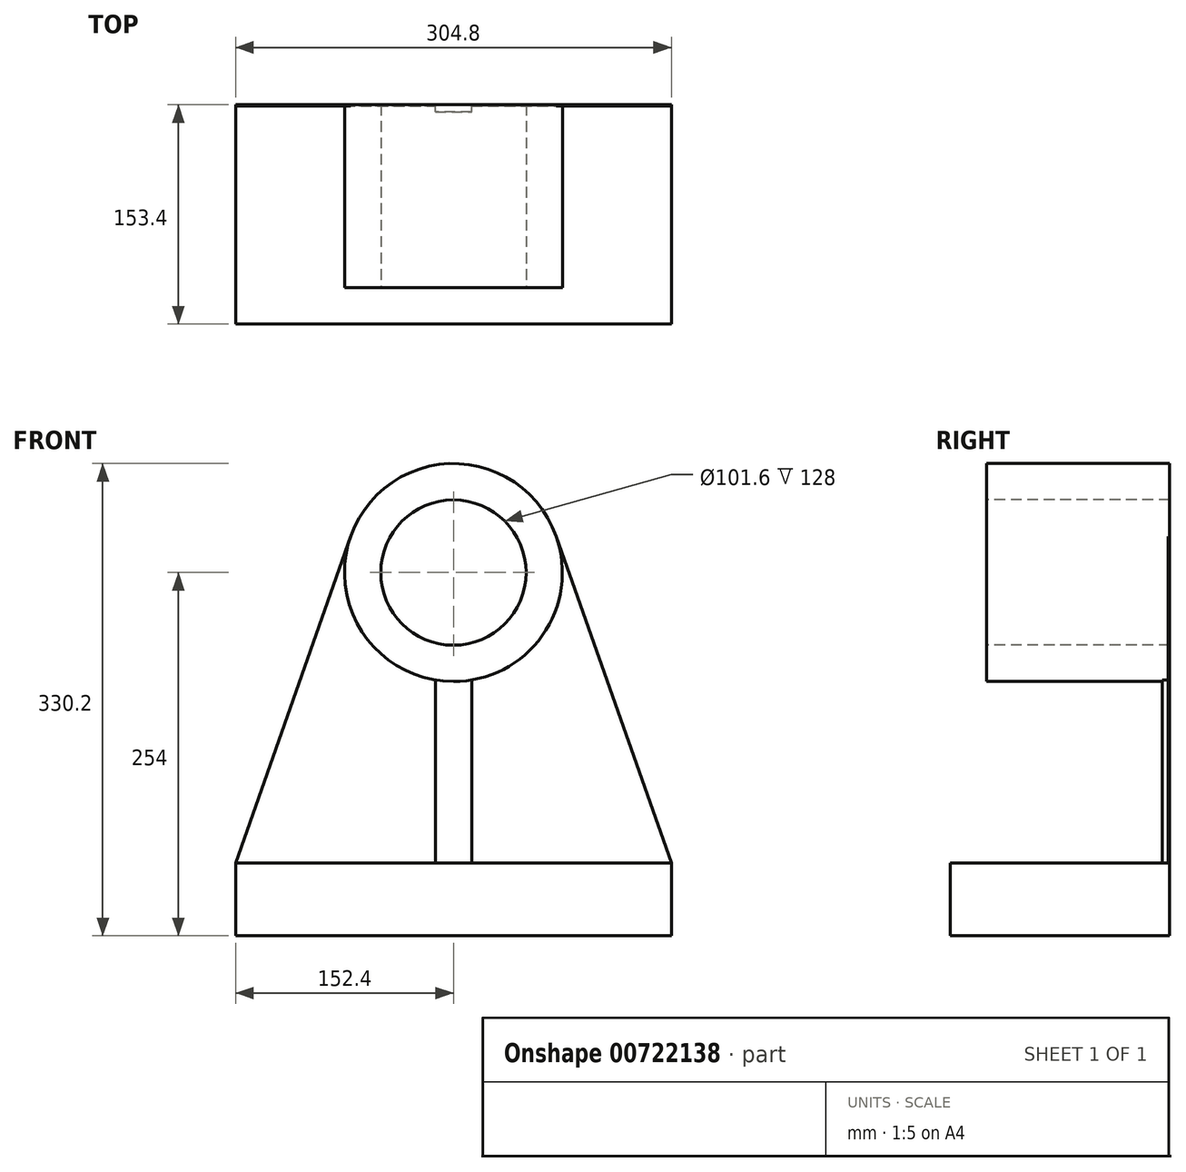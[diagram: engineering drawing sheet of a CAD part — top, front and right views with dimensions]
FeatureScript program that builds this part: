
annotation { "Feature Type Name" : "Feature", "Feature Type Description" : "" }
export const myFeature = defineFeature(function(context is Context, id is Id, definition is map)
    precondition{}
    {
        {
            assignVariable(context, id + "F0", {"name" : "C", "anyValue" : 1});
        }
        {
            var Q0;
            Q0=qCreatedBy(makeId("Front.planeOp"),FACE);
            var sketch = newSketch(context, id + "F1", { "sketchPlane" : qUnion([Q0])});
            skLineSegment(sketch, "E0.bottom", {"start": v(0, 0) * mm, "end": v(-304.8, 0) * mm});
            skLineSegment(sketch, "E0.left", {"start": v(0, 0) * mm, "end": v(0, 50.8) * mm});
            skLineSegment(sketch, "E0.right", {"start": v(-304.8, 0) * mm, "end": v(-304.8, 50.8) * mm});
            skLineSegment(sketch, "E1", {"start": v(0, 50.8) * mm, "end": v(-80.53, 279.33) * mm});
            skArc(sketch, "E2", {"start": v(-80.53, 279.33) * mm, "mid": v(-152.4, 330.2) * mm, "end": v(-224.27, 279.33) * mm});
            skLineSegment(sketch, "E3", {"start": v(-304.8, 50.8) * mm, "end": v(-224.27, 279.33) * mm});
            skLineSegment(sketch, "E4", {"start": v(-152.4, 254) * mm, "end": v(-152.4, 0) * mm, "construction": true});
            skSolve(sketch);
        }
        {
            var Q0;
            Q0=qSketchRegion(id+"F1",true);
            extrude(context, id + "F2", {"entities" : qUnion([Q0]), "depth" : (getVariable(context, 'C')) * mm, "offsetDistance" : 25.4 * mm});
        }
        {
            var Q0;
            Q0=makeQuery(id+"F2.opExtrude","CAP_FACE",FACE,{"disambiguationData":[OSD([sQuery(id+"F1.wireOp",EDGE,"E0.bottom"),sQuery(id+"F1.wireOp",EDGE,"E0.left"),sQuery(id+"F1.wireOp",EDGE,"E0.right"),sQuery(id+"F1.wireOp",EDGE,"E1"),sQuery(id+"F1.wireOp",EDGE,"E2"),sQuery(id+"F1.wireOp",EDGE,"E3")])],"isStart":false});
            var sketch = newSketch(context, id + "F3", { "sketchPlane" : qUnion([Q0])});
            skLineSegment(sketch, "E5.bottom", {"start": v(0, 0) * mm, "end": v(-304.8, 0) * mm});
            skLineSegment(sketch, "E5.top", {"start": v(0, 50.8) * mm, "end": v(-304.8, 50.8) * mm});
            skLineSegment(sketch, "E5.left", {"start": v(0, 0) * mm, "end": v(0, 50.8) * mm});
            skLineSegment(sketch, "E5.right", {"start": v(-304.8, 0) * mm, "end": v(-304.8, 50.8) * mm});
            skSolve(sketch);
        }
        {
            var Q0;
            Q0=qSketchRegion(id+"F3",true);
            extrude(context, id + "F4", {"entities" : qUnion([Q0]), "operationType" : NewBodyOperationType.ADD, "depth" : 152.4 * mm, "offsetDistance" : 25.4 * mm});
        }
        {
            var Q0;
            Q0=makeQuery(id+"F2.opExtrude","CAP_FACE",FACE,{"disambiguationData":[OSD([sQuery(id+"F1.wireOp",EDGE,"E0.bottom"),sQuery(id+"F1.wireOp",EDGE,"E0.left"),sQuery(id+"F1.wireOp",EDGE,"E0.right"),sQuery(id+"F1.wireOp",EDGE,"E1"),sQuery(id+"F1.wireOp",EDGE,"E2"),sQuery(id+"F1.wireOp",EDGE,"E3")])],"isStart":false});
            var sketch = newSketch(context, id + "F5", { "sketchPlane" : qUnion([Q0])});
            skLineSegment(sketch, "E6", {"start": v(-152.4, 50.8) * mm, "end": v(-152.4, 254) * mm, "construction": true});
            skLineSegment(sketch, "E7.bottom", {"start": v(-165.1, 50.8) * mm, "end": v(-139.7, 50.8) * mm});
            skLineSegment(sketch, "E7.top", {"start": v(-165.1, 254) * mm, "end": v(-139.7, 254) * mm});
            skLineSegment(sketch, "E7.left", {"start": v(-165.1, 50.8) * mm, "end": v(-165.1, 254) * mm});
            skLineSegment(sketch, "E7.right", {"start": v(-139.7, 50.8) * mm, "end": v(-139.7, 254) * mm});
            skSolve(sketch);
        }
        {
            var Q0;
            Q0=qSketchRegion(id+"F5",true);
            extrude(context, id + "F6", {"entities" : qUnion([Q0]), "operationType" : NewBodyOperationType.ADD, "depth" : (5 - getVariable(context, 'C')) * mm, "offsetDistance" : 25.4 * mm});
        }
        {
            var Q0;
            Q0=makeQuery(id+"F2.opExtrude","CAP_FACE",FACE,{"disambiguationData":[OSD([sQuery(id+"F1.wireOp",EDGE,"E0.bottom"),sQuery(id+"F1.wireOp",EDGE,"E0.left"),sQuery(id+"F1.wireOp",EDGE,"E0.right"),sQuery(id+"F1.wireOp",EDGE,"E1"),sQuery(id+"F1.wireOp",EDGE,"E2"),sQuery(id+"F1.wireOp",EDGE,"E3")])],"isStart":false});
            var sketch = newSketch(context, id + "F7", { "sketchPlane" : qUnion([Q0])});
            skCircle(sketch, "E8", {"center": v(-152.4, 254) * mm, "radius": 76.2 * mm});
            skSolve(sketch);
        }
        {
            var Q0;
            Q0=qSketchRegion(id+"F7",true);
            extrude(context, id + "F8", {"entities" : qUnion([Q0]), "operationType" : NewBodyOperationType.ADD, "depth" : 127 * mm, "offsetDistance" : 25.4 * mm});
        }
        {
            var Q0;
            Q0=makeQuery(id+"F8.opExtrude","CAP_FACE",FACE,{"disambiguationData":[OSD([sQuery(id+"F7.wireOp",EDGE,"E8")])],"isStart":false});
            var sketch = newSketch(context, id + "F9", { "sketchPlane" : qUnion([Q0])});
            skCircle(sketch, "E9", {"center": v(-152.4, 254) * mm, "radius": 50.8 * mm});
            skLineSegment(sketch, "E10", {"start": v(-152.4, 304.8) * mm, "end": v(-152.4, 330.2) * mm, "construction": true});
            skSolve(sketch);
        }
        {
            var Q0;
            Q0=makeQuery(id+"F9.imprint","IMPRINT",FACE,{"disambiguationData":[TD([[makeQuery(id+"F9.imprint","IMPRINT",EDGE,{"derivedFrom":sQuery(id+"F9.wireOp",EDGE,"E9")}),1.0]])]});
            extrude(context, id + "F10", {"entities" : qUnion([Q0]), "operationType" : NewBodyOperationType.REMOVE, "endBound" : BoundingType.THROUGH_ALL, "oppositeDirection" : true, "depth" : 25.4 * mm, "offsetDistance" : 25.4 * mm});
        }
    });
